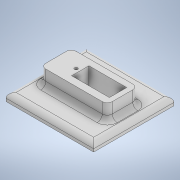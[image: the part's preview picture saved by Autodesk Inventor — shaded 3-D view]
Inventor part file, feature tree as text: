
AUTODESK INVENTOR PART (.ipt)
format: ipt  version: 2020 (Build 240168000, 168)  size: 177,152 bytes
history: native  units: in
note: dims shown in document units (in); Inventor stores cm internally (conversion verified against a paired STEP export)
features: extrude x4, sketch x3, fillet x1
ambient origin geometry x8: Origin, YZ Plane, XZ Plane, XY Plane, X Axis, Y Axis, Z Axis, Center Point
bodies: Solid1 (feature_tree)
feature tree (8):
  sketch  "Sketch1"  dims[d0=0.9449in d1=0.4331in]
  extrude  "Extrusion1"  Depth=0.4331in
  extrude  "Extrusion2"  Depth=0.7874in
  fillet  "Fillet1"  Radius=0.3937in
  extrude  "Extrusion3"  Depth=0.5906in TaperAngle=0.0deg
  extrude  "Extrusion4"  Depth=0.1969in TaperAngle=0.0deg
  sketch  "Sketch2"  dims[d2=0.7874in d3=0.7874in d4=0.3937in]
  sketch  "Sketch3"  dims[d6=0.3937in d7=0.5906in d8=0.0in d9=0.1969in d10=0.0in d11=0.125in d12=0.9843in d13=0.0in d14=0.0984in d15=0.0984in d16=0.0787in d17=0.0984in d18=0.0in]
